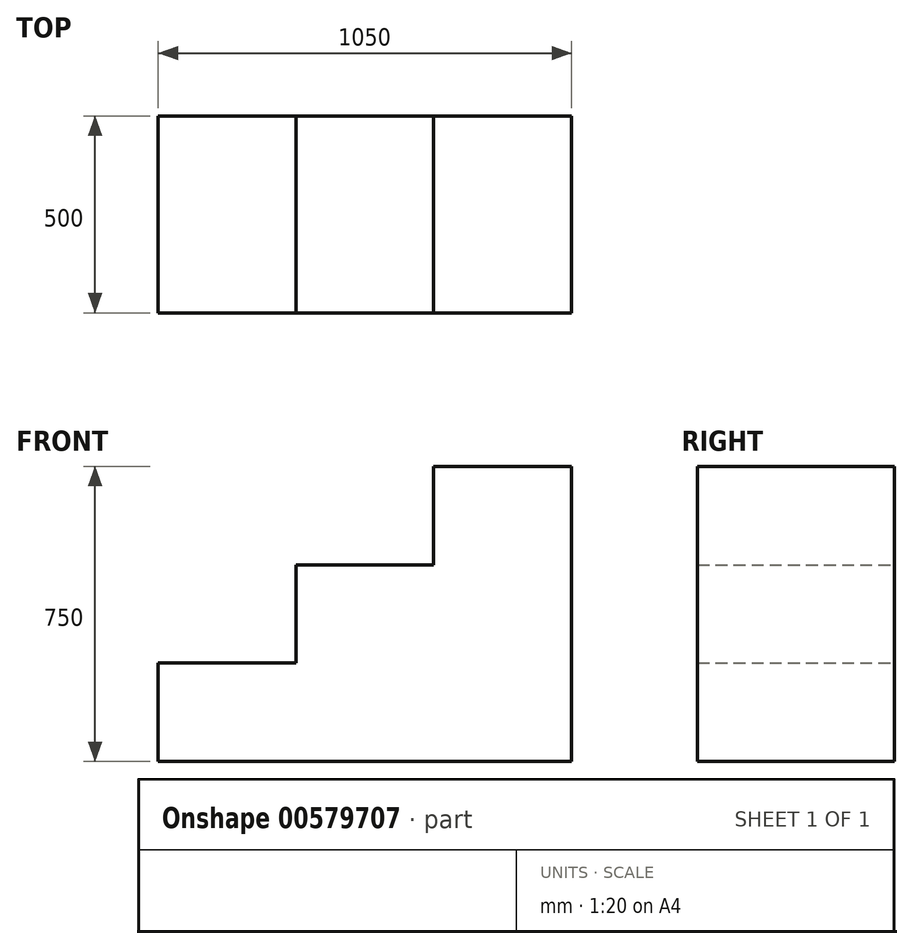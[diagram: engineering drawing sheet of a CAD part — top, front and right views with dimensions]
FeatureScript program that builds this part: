
annotation { "Feature Type Name" : "Feature", "Feature Type Description" : "" }
export const myFeature = defineFeature(function(context is Context, id is Id, definition is map)
    precondition{}
    {
        {
            var Q0;
            Q0=qCreatedBy(makeId("Front.planeOp"),FACE);
            var sketch = newSketch(context, id + "F0", { "sketchPlane" : qUnion([Q0])});
            skLineSegment(sketch, "E0", {"start": v(0, 0) * mm, "end": v(1050, 0) * mm});
            skLineSegment(sketch, "E1", {"start": v(1050, 0) * mm, "end": v(1050, 750) * mm});
            skLineSegment(sketch, "E2", {"start": v(1050, 750) * mm, "end": v(700, 750) * mm});
            skLineSegment(sketch, "E3", {"start": v(700, 750) * mm, "end": v(700, 500) * mm});
            skLineSegment(sketch, "E4", {"start": v(700, 500) * mm, "end": v(350, 500) * mm});
            skLineSegment(sketch, "E5", {"start": v(350, 500) * mm, "end": v(350, 250) * mm});
            skLineSegment(sketch, "E6", {"start": v(350, 250) * mm, "end": v(0, 250) * mm});
            skLineSegment(sketch, "E7", {"start": v(0, 250) * mm, "end": v(0, 0) * mm});
            skLineSegment(sketch, "E8", {"start": v(0, 0) * mm, "end": v(500, 0) * mm});
            skSolve(sketch);
        }
        {
            var Q0;
            Q0=makeQuery(id+"F0.imprint","IMPRINT",FACE,{"disambiguationData":[TD([[makeQuery(id+"F0.imprint","IMPRINT",EDGE,{"derivedFrom":sQuery(id+"F0.wireOp",EDGE,"E0")}),1.0]])]});
            extrude(context, id + "F1", {"entities" : qUnion([Q0]), "depth" : 500 * mm, "offsetDistance" : 25 * mm});
        }
    });
